# Revit family: NBS_Allermuir_OffcChrs_Famiglia-en-us_LowBack
name_source: partatom
category: Furniture
revit_build: Autodesk Revit 2016 (Build: 20151007_0715(x64)
units: mm (PartAtom-declared; Revit-internal decimal feet)

## family parameters
Always vertical = Yes
Cut with Voids When Loaded = No
Room Calculation Point = No
Shared = No
Work Plane-Based = No

## types (3) — shared parameters
AssetType = Moveable
Category = Pr_40_50_12_57:Office chairs
CodePerformance = ANSI/BIFMA X5.1: 2011
DurationUnit = year
EnvironmentalProductDeclaration = http://www.thesenatorgroup.com
ExpectedLife = 10
FrameMountingMaterial = NBS_Concept
IfcExportAs = IfcFurnitureType
IfcExportType = CHAIR
IsBuiltIn = No
ManufacturerName = Allermuir
ManufacturerURL = http://www.thesenatorgroup.com
ModelReference = Famiglia low
NBSCertification = www.nationalbimlibrary.com/cert/w0q2kw44
NBSDescription = Office chairs
NBSReference = 45-35-20/330
NominalDepth = 25 "
NominalHeight = 32 "
NominalLength = 23 "
NominalWidth = 25 "
OmniClassCode = 22-12 52 23
OmniClassTitle = Office Seating
OmniClassVersion = Table 22 2012-05-16
ProductInformation = http://www.thesenatorgroup.com
SeatBaseMaterial = NBS_Concept
SeatFrameMaterial = NBS_Concept
SeatingSeatMaterial = NBS_Concept
SeatsAndBacksColourOptions = Black, White, Red, Light Grey, Dark Grey, Cream
SeatsAndBacksFinish = Fully upholstered
SeatsAndBacksFinishOptions = Decorative railroad stitch detail to perimeter seam,Two-tone upholstery
SeatsAndBacksMaterial = Molded foam
StandardsDurability = ANSI/BIFMA X5.1: 2011
StandardsSafetyRequirements = ANSI/BIFMA X5.1: 2011
Status = UNSET
Uniclass2015Code = Pr_40_50_12_57
Uniclass2015Title = Office chairs
Uniclass2015Version = Products v1.9
Version = 1
WarrantyDescription = Allermuir warrant that its manufactured products are free from manufacturing defects in materials or workmanship for a period of ten years
WarrantyDurationParts = 10
WarrantyDurationUnit = year
zero-valued in all types: HighestSeatingHeight, LowestSeatingHeight

## per-type parameters (varying)
| type | BIMObjectName | Description | Features | FrameColour | FrameColourOptions | FrameFinish | FrameFinishOptions | FrameMaterials | IntegralAccessories | Name | OfficeChairBase | SeatingHeight | Size |
| FMG101 | NBS_Allermuir_OfficeChairs_Famiglia_FMG101-US | Low back on a 4 leg frame with castors | Molded foam construction, fully upholstered, tubular steel frame on 2.5" hard wheel castors finished in polished chrome, tubular steel frame available in slate grey powder coat, 2" soft wheel castors | Chrome | Slate grey | Polished | Also available in slate grey powder coat | Tubular steel | 2.5" hard wheel castors | OfficeChairs_Famiglia_FMG101-US_Allermuir | NBS_Allermuir_OffcChrs_Famiglia_4LegFrameOnCastors | 18 " | 24.75 x 31.5 x 23.25" |
| FMG102 | NBS_Allermuir_OfficeChairs_Famiglia_FMG102-US | Low back on a 4 leg frame | Molded foam construction, fully upholstered, tubular steel frame with wire supports finished in polished chrome, plastic glides, tubular Steel frame with wire supports available in slate grey powder coat, plastic glides with felt | Chrome | Slate grey | Polished | Also available in slate grey powder coat | Tubular steel | Plastic glides | OfficeChairs_Famiglia_FMG102-US_Allermuir | NBS_Allermuir_OffcChrs_Famiglia_4LegFrameLow | 19 " | 24.75 x 32 x 23.25" |
| FMG103 | NBS_Allermuir_OfficeChairs_Famiglia_FMG103-US | Low back with wood legs | Molded foam construction, fully upholstered,aluminum leg connector frame finished in slate grey powder coat, solid ash legs with a clear finish, plastic glides, solid ash legs can be stained or color washed, plastic glides with felt | Ash | Can be stained or color washed | Clear | Can be stained or color washed | Solid ash | Plastic glides | OfficeChairs_Famiglia_FMG103-US_Allermuir | NBS_Allermuir_OffcChrs_Famiglia_WoodLegs | 19 " | 24.75 x 32 x 23.25" |

note: column(s) folded — value = type name in every type: ModelNumber

## geometry (parser evidence)
native form markers: Sweep x13
no freeform markers — native parametric forms only
